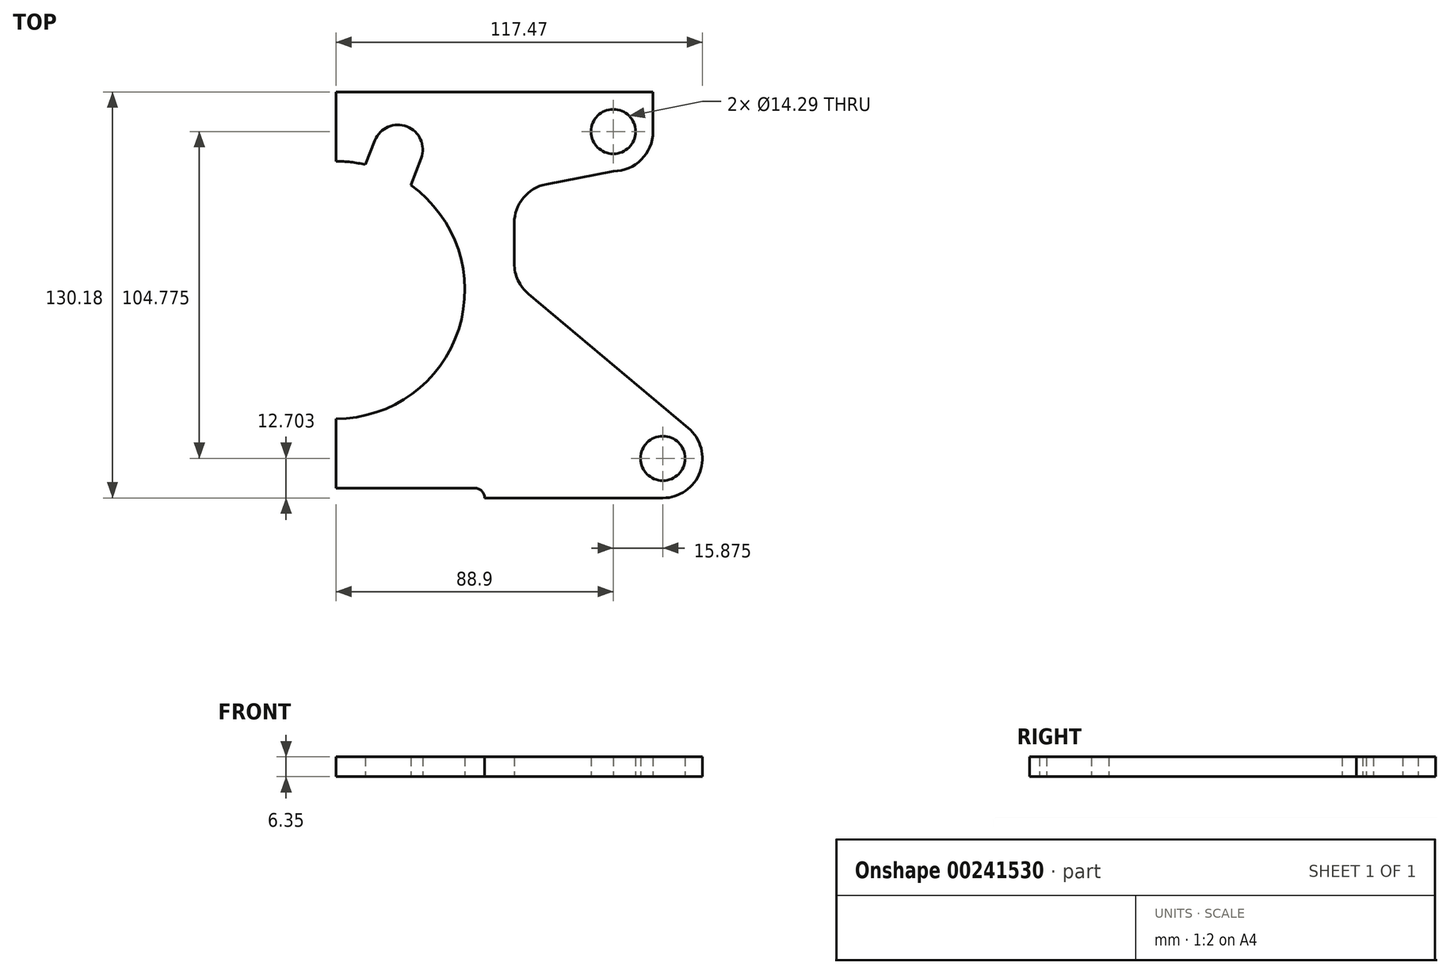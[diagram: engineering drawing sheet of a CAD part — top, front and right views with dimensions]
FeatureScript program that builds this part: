
annotation { "Feature Type Name" : "Feature", "Feature Type Description" : "" }
export const myFeature = defineFeature(function(context is Context, id is Id, definition is map)
    precondition{}
    {
        {
            var Q0;
            Q0=qCreatedBy(makeId("Top.planeOp"),FACE);
            var sketch = newSketch(context, id + "F0", { "sketchPlane" : qUnion([Q0])});
            skLineSegment(sketch, "E0.bottom", {"start": v(0, 55.82) * mm, "end": v(88.9, 55.82) * mm});
            skLineSegment(sketch, "E0.left", {"start": v(0, 55.82) * mm, "end": v(0, -71.18) * mm});
            skLineSegment(sketch, "E1.bottom", {"start": v(88.9, 55.82) * mm, "end": v(101.6, 55.82) * mm});
            skLineSegment(sketch, "E1.top", {"start": v(88.9, 30.42) * mm, "end": v(88.9, 30.42) * mm});
            skLineSegment(sketch, "E1.right", {"start": v(101.6, 55.82) * mm, "end": v(101.6, 43.12) * mm});
            skCircle(sketch, "E2", {"center": v(88.9, 43.12) * mm, "radius": 7.14 * mm});
            skPoint(sketch, "E3.visualSharp", {"position": v(101.6, 30.42) * mm});
            skArc(sketch, "E3.filletArc", {"start": v(88.9, 30.42) * mm, "mid": v(97.88, 34.14) * mm, "end": v(101.6, 43.12) * mm});
            skLineSegment(sketch, "E4", {"start": v(88.9, 30.42) * mm, "end": v(67.43, 26.24) * mm});
            skPoint(sketch, "E5.newPointB", {"position": v(57.15, 55.82) * mm});
            skArc(sketch, "E5.filletArc", {"start": v(67.43, 26.24) * mm, "mid": v(60.05, 21.86) * mm, "end": v(57.15, 13.78) * mm});
            skLineSegment(sketch, "E6", {"start": v(47.63, -74.36) * mm, "end": v(47.63, -74.36) * mm});
            skLineSegment(sketch, "E7", {"start": v(44.45, -71.18) * mm, "end": v(0, -71.18) * mm});
            skPoint(sketch, "E8.visualSharp", {"position": v(47.63, -71.18) * mm});
            skArc(sketch, "E8.filletArc", {"start": v(47.63, -74.36) * mm, "mid": v(46.7, -72.11) * mm, "end": v(44.45, -71.18) * mm});
            skArc(sketch, "E9.MirrorCS", {"start": v(-47.63, -74.36) * mm, "mid": v(-46.7, -72.11) * mm, "end": v(-44.45, -71.18) * mm});
            skLineSegment(sketch, "E10.MirrorCS", {"start": v(-88.9, 55.82) * mm, "end": v(-101.6, 55.82) * mm});
            skLineSegment(sketch, "E11.MirrorCS", {"start": v(-44.45, -71.18) * mm, "end": v(0, -71.18) * mm});
            skPoint(sketch, "E12.MirrorP", {"position": v(-104.58, -48.96) * mm});
            skLineSegment(sketch, "E13.MirrorCS", {"start": v(-88.9, 30.42) * mm, "end": v(-67.43, 26.24) * mm});
            skArc(sketch, "E14.MirrorCS", {"start": v(-67.43, 26.24) * mm, "mid": v(-60.05, 21.86) * mm, "end": v(-57.15, 13.78) * mm});
            skArc(sketch, "E15.MirrorCS", {"start": v(-88.9, 30.42) * mm, "mid": v(-97.88, 34.14) * mm, "end": v(-101.6, 43.12) * mm});
            skPoint(sketch, "E16.MirrorP", {"position": v(-57.15, 55.82) * mm});
            skLineSegment(sketch, "E17.MirrorCS", {"start": v(-88.9, 30.42) * mm, "end": v(-88.9, 30.42) * mm});
            skPoint(sketch, "E18.MirrorP", {"position": v(-101.6, 30.42) * mm});
            skPoint(sketch, "E19.MirrorP", {"position": v(-57.15, -9.27) * mm});
            skCircle(sketch, "E20.MirrorC", {"center": v(-88.9, 43.12) * mm, "radius": 7.14 * mm});
            skLineSegment(sketch, "E21.MirrorCS", {"start": v(-101.6, 55.82) * mm, "end": v(-101.6, 43.12) * mm});
            skLineSegment(sketch, "E22.MirrorCS", {"start": v(-47.63, -74.36) * mm, "end": v(-47.63, -74.36) * mm});
            skPoint(sketch, "E23.MirrorP", {"position": v(-47.63, -71.18) * mm});
            skLineSegment(sketch, "E24.MirrorCS", {"start": v(0, 55.82) * mm, "end": v(-88.9, 55.82) * mm});
            skArc(sketch, "E25", {"start": v(9.39, 32.51) * mm, "mid": v(-17.01, -45.29) * mm, "end": v(24, 25.9) * mm});
            skArc(sketch, "E26", {"start": v(27.28, 34.52) * mm, "mid": v(22.74, 44.74) * mm, "end": v(12.48, 40.28) * mm});
            skLineSegment(sketch, "E27", {"start": v(12.48, 40.28) * mm, "end": v(9.39, 32.51) * mm});
            skLineSegment(sketch, "E28", {"start": v(27.28, 34.52) * mm, "end": v(24, 25.9) * mm});
            skLineSegment(sketch, "E29.bottom", {"start": v(104.78, -74.36) * mm, "end": v(104.78, -74.36) * mm});
            skLineSegment(sketch, "E30", {"start": v(47.63, -74.36) * mm, "end": v(104.78, -74.36) * mm});
            skArc(sketch, "E31.filletArc", {"start": v(117.48, -61.9) * mm, "mid": v(117.47, -61.83) * mm, "end": v(117.43, -61.77) * mm});
            skLineSegment(sketch, "E32.MirrorCS", {"start": v(-47.63, -74.36) * mm, "end": v(-104.78, -74.36) * mm});
            skArc(sketch, "E33.MirrorCS", {"start": v(-104.78, -74.36) * mm, "mid": v(-111.35, -72.52) * mm, "end": v(-116.03, -67.54) * mm});
            skCircle(sketch, "E34.MirrorC", {"center": v(-104.78, -61.66) * mm, "radius": 7.14 * mm});
            skPoint(sketch, "E35.MirrorP", {"position": v(-117.47, -49.12) * mm});
            skCircle(sketch, "E36", {"center": v(-58.74, -58.48) * mm, "radius": 9.53 * mm});
            skArc(sketch, "E37", {"start": v(-112.94, -51.93) * mm, "mid": v(-116.7, -66) * mm, "end": v(-104.78, -74.36) * mm});
            skLineSegment(sketch, "E38", {"start": v(-112.94, -51.93) * mm, "end": v(-61.69, -8.92) * mm});
            skLineSegment(sketch, "E39", {"start": v(-57.15, 13.78) * mm, "end": v(-57.15, 0.8) * mm});
            skPoint(sketch, "E40.visualSharp", {"position": v(-57.15, -5.12) * mm});
            skArc(sketch, "E40.filletArc", {"start": v(-61.69, -8.92) * mm, "mid": v(-58.34, -4.56) * mm, "end": v(-57.15, 0.8) * mm});
            skLineSegment(sketch, "E41.MirrorCS", {"start": v(112.94, -51.93) * mm, "end": v(61.69, -8.92) * mm});
            skLineSegment(sketch, "E42.MirrorCS", {"start": v(57.15, 13.78) * mm, "end": v(57.15, 0.8) * mm});
            skArc(sketch, "E43.MirrorCS", {"start": v(61.69, -8.92) * mm, "mid": v(58.34, -4.56) * mm, "end": v(57.15, 0.8) * mm});
            skPoint(sketch, "E44.MirrorP", {"position": v(57.15, -5.12) * mm});
            skArc(sketch, "E45.MirrorCS", {"start": v(112.94, -51.93) * mm, "mid": v(116.7, -66) * mm, "end": v(104.78, -74.36) * mm});
            skCircle(sketch, "E46.MirrorC", {"center": v(104.78, -61.66) * mm, "radius": 7.14 * mm});
            skSolve(sketch);
        }
        {
            var Q0;
            Q0=makeQuery(id+"F0.imprint","IMPRINT",FACE,{"disambiguationData":[TD([[makeQuery(id+"F0.imprint","IMPRINT",EDGE,{"derivedFrom":sQuery(id+"F0.wireOp",EDGE,"E9.MirrorCS")}),1.0]])]});
            var Q1;
            {var subQ7=sQuery(id+"F0.wireOp",EDGE,"E0.bottom");Q1=makeQuery(id+"F0.imprint","IMPRINT",FACE,{"disambiguationData":[TD([[makeQuery(id+"F0.imprint","IMPRINT",EDGE,{"derivedFrom":subQ7}),-1.0]])]});}
            extrude(context, id + "F1", {"entities" : qUnion([Q0, Q1]), "depth" : 6.35 * mm});
        }
    });
